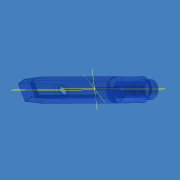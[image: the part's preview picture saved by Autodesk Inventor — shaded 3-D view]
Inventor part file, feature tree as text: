
AUTODESK INVENTOR PART (.ipt)
format: ipt  version: 2013 (Build 170138000, 138)  size: 179,200 bytes
history: native  units: mm
features: sketch x8, other x6, fillet x5, hole x4, projected_geometry x4, extrude x3, chamfer x2
ambient origin geometry x8: Origin, YZ Plane, XZ Plane, XY Plane, X Axis, Y Axis, Z Axis, Center Point
bodies: Volumenkörper1 (feature_tree)
feature tree (32):
  other  "Drehung2"
  extrude  "Extrusion1"  TaperAngle=90.0deg  [1 undecoded]
  chamfer  "Fase1"  Distance=1.0mm
  chamfer  "Fase2"  Distance=31.75mm
  fillet  "Rundung1"  Radius=2.5mm
  fillet  "Rundung2"  Radius=0.25mm
  fillet  "Rundung3"  Radius=0.25mm
  fillet  "Rundung4"  Radius=0.25mm
  extrude  "Extrusion2"  Depth=8.0mm TaperAngle=0.0deg
  extrude  "Extrusion3"  Depth=0.25mm
  fillet  "Rundung5"  Radius=27.0mm
  other  "Arbeitsachse12"
  hole  "Bohrung11"  [1 undecoded]
  hole  "Bohrung12"  [1 undecoded]
  hole  "Bohrung13"  [1 undecoded]
  other  "Arbeitsachse13"
  other  "Arbeitsachse14"
  other  "Arbeitspunkt4"
  other  "Arbeitsachse16"
  hole  "Bohrung15"  [1 undecoded]
  sketch  "Skizze1"  dims[d25=3.25mm d31=90.0deg]
  sketch  "Skizze5"  dims[d63=4.0mm d64=1.0mm d66=1.15mm d67=31.75mm d68=0.0mm d69=2.5mm]
  sketch  "Skizze11"  dims[d85=5.0mm d86=0.5mm d87=45.0deg]
  projected_geometry  "Projizierte Kontur4"
  sketch  "Skizze18"  dims[d88=5.0mm d89=0.5mm d90=45.0deg d91=0.25mm d92=0.25mm d93=0.25mm]
  projected_geometry  "Projizierte Kontur5"
  projected_geometry  "Projizierte Kontur6"
  sketch  "Skizze19"  dims[d94=0.25mm d111=8.0mm d112=0.0mm]
  sketch  "Skizze20"  dims[d149=3.0mm d150=0.0mm d151=0.25mm d153=27.0mm]
  sketch  "Skizze21"  dims[d154=9.0mm d155=3.0mm]
  sketch  "Skizze23"  dims[d156=2.5mm d157=3.2mm d158=6.0mm d159=4.0mm d160=2.0mm d161=90.0deg d162=0.15mm d163=0.0mm d164=2.2mm d165=6.0mm d166=4.0mm d167=2.0mm d168=90.0deg d169=1.0mm d170=0.0mm d171=4.0mm d172=6.0mm d173=4.0mm d174=2.0mm d175=90.0deg d176=11.0mm d177=0.0mm d185=0.8mm d186=6.0mm d187=4.0mm d188=2.0mm d189=90.0deg d190=9.0mm d191=0.0mm d138=1.0mm d139=1.0mm]
  projected_geometry  "Projizierte Kontur7"
note: 5 required parameter values undecoded (feature->parameter linkage not recoverable at this tier; creation-order binding heuristic only, values carry confidence <= 0.55)
